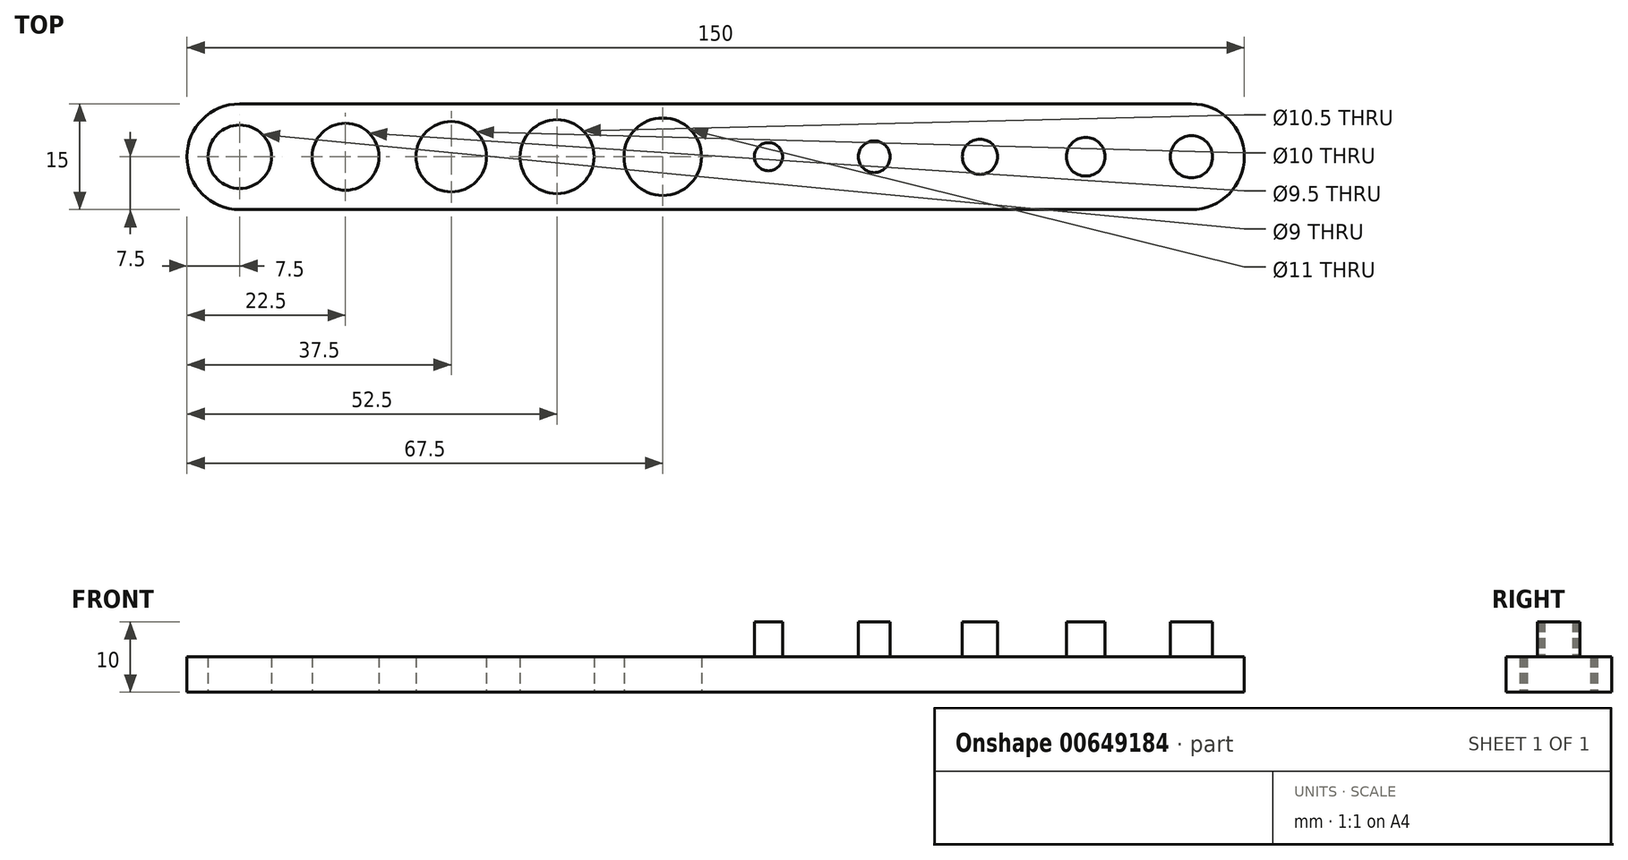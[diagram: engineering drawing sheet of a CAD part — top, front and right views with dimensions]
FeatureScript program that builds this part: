
annotation { "Feature Type Name" : "Feature", "Feature Type Description" : "" }
export const myFeature = defineFeature(function(context is Context, id is Id, definition is map)
    precondition{}
    {
        {
            var Q0;
            Q0=qCreatedBy(makeId("Top.planeOp"),FACE);
            var sketch = newSketch(context, id + "F0", { "sketchPlane" : qUnion([Q0])});
            skLineSegment(sketch, "E0.bottom", {"start": v(75, 7.5) * mm, "end": v(-75, 7.5) * mm});
            skLineSegment(sketch, "E0.top", {"start": v(75, -7.5) * mm, "end": v(-75, -7.5) * mm});
            skLineSegment(sketch, "E0.left", {"start": v(75, 7.5) * mm, "end": v(75, -7.5) * mm});
            skLineSegment(sketch, "E0.right", {"start": v(-75, 7.5) * mm, "end": v(-75, -7.5) * mm});
            skPoint(sketch, "E0.middle", {"position": v(0, 0) * mm});
            skLineSegment(sketch, "E1", {"start": v(-75, 0) * mm, "end": v(-60, 0) * mm, "construction": true});
            skPoint(sketch, "E1.endSnap0", {"position": v(-75, 0) * mm});
            skLineSegment(sketch, "E2", {"start": v(-60, 0) * mm, "end": v(-45, 0) * mm, "construction": true});
            skLineSegment(sketch, "E3", {"start": v(-45, 0) * mm, "end": v(-30, 0) * mm, "construction": true});
            skLineSegment(sketch, "E4", {"start": v(-30, 0) * mm, "end": v(-15, 0) * mm, "construction": true});
            skLineSegment(sketch, "E5", {"start": v(-15, 0) * mm, "end": v(0, 0) * mm, "construction": true});
            skCircle(sketch, "E6", {"center": v(-67.5, 0) * mm, "radius": 4.5 * mm});
            skCircle(sketch, "E7", {"center": v(-52.5, 0) * mm, "radius": 4.75 * mm});
            skCircle(sketch, "E8", {"center": v(-37.5, 0) * mm, "radius": 5 * mm});
            skCircle(sketch, "E9", {"center": v(-22.5, 0) * mm, "radius": 5.25 * mm});
            skCircle(sketch, "E10", {"center": v(-7.5, 0) * mm, "radius": 5.5 * mm});
            skSolve(sketch);
        }
        {
            var Q0;
            Q0=qSketchRegion(id+"F0",true);
            extrude(context, id + "F1", {"entities" : qUnion([Q0]), "depth" : 5 * mm});
        }
        {
            var Q0;
            Q0=makeQuery(id+"F1.opExtrude","SWEPT_EDGE",EDGE,{"disambiguationData":[OSD([sQuery(id+"F0.wireOp",EDGE,"E0.top"),sQuery(id+"F0.wireOp",EDGE,"E0.right")])]});
            var Q1;
            Q1=makeQuery(id+"F1.opExtrude","SWEPT_EDGE",EDGE,{"disambiguationData":[OSD([sQuery(id+"F0.wireOp",EDGE,"E0.bottom"),sQuery(id+"F0.wireOp",EDGE,"E0.right")])]});
            var Q2;
            Q2=makeQuery(id+"F1.opExtrude","SWEPT_EDGE",EDGE,{"disambiguationData":[OSD([sQuery(id+"F0.wireOp",EDGE,"E0.top"),sQuery(id+"F0.wireOp",EDGE,"E0.left")])]});
            var Q3;
            Q3=makeQuery(id+"F1.opExtrude","SWEPT_EDGE",EDGE,{"disambiguationData":[OSD([sQuery(id+"F0.wireOp",EDGE,"E0.bottom"),sQuery(id+"F0.wireOp",EDGE,"E0.left")])]});
            fillet(context, id + "F2", {"entities" : qUnion([Q0, Q1, Q2, Q3]), "radius" : 7.5 * mm, "tangentPropagation" : true, "allowEdgeOverflow" : false});
        }
        {
            var Q0;
            Q0=qCreatedBy(makeId("Top.planeOp"),FACE);
            var sketch = newSketch(context, id + "F3", { "sketchPlane" : qUnion([Q0])});
            skLineSegment(sketch, "E11", {"start": v(0, 0) * mm, "end": v(15, 0) * mm, "construction": true});
            skLineSegment(sketch, "E12", {"start": v(15, 0) * mm, "end": v(30, 0) * mm, "construction": true});
            skLineSegment(sketch, "E13", {"start": v(30, 0) * mm, "end": v(45, 0) * mm, "construction": true});
            skLineSegment(sketch, "E14", {"start": v(45, 0) * mm, "end": v(60, 0) * mm, "construction": true});
            skLineSegment(sketch, "E15", {"start": v(60, 0) * mm, "end": v(75, 0) * mm, "construction": true});
            skCircle(sketch, "E16", {"center": v(67.5, 0) * mm, "radius": 3 * mm});
            skCircle(sketch, "E17", {"center": v(37.5, 0) * mm, "radius": 2.5 * mm});
            skCircle(sketch, "E18", {"center": v(52.5, 0) * mm, "radius": 2.75 * mm});
            skCircle(sketch, "E19", {"center": v(22.5, 0) * mm, "radius": 2.25 * mm});
            skCircle(sketch, "E20", {"center": v(7.5, 0) * mm, "radius": 2 * mm});
            skSolve(sketch);
        }
        {
            var Q0;
            Q0=qSketchRegion(id+"F3",true);
            extrude(context, id + "F4", {"entities" : qUnion([Q0]), "operationType" : NewBodyOperationType.ADD, "depth" : 10 * mm});
        }
    });
